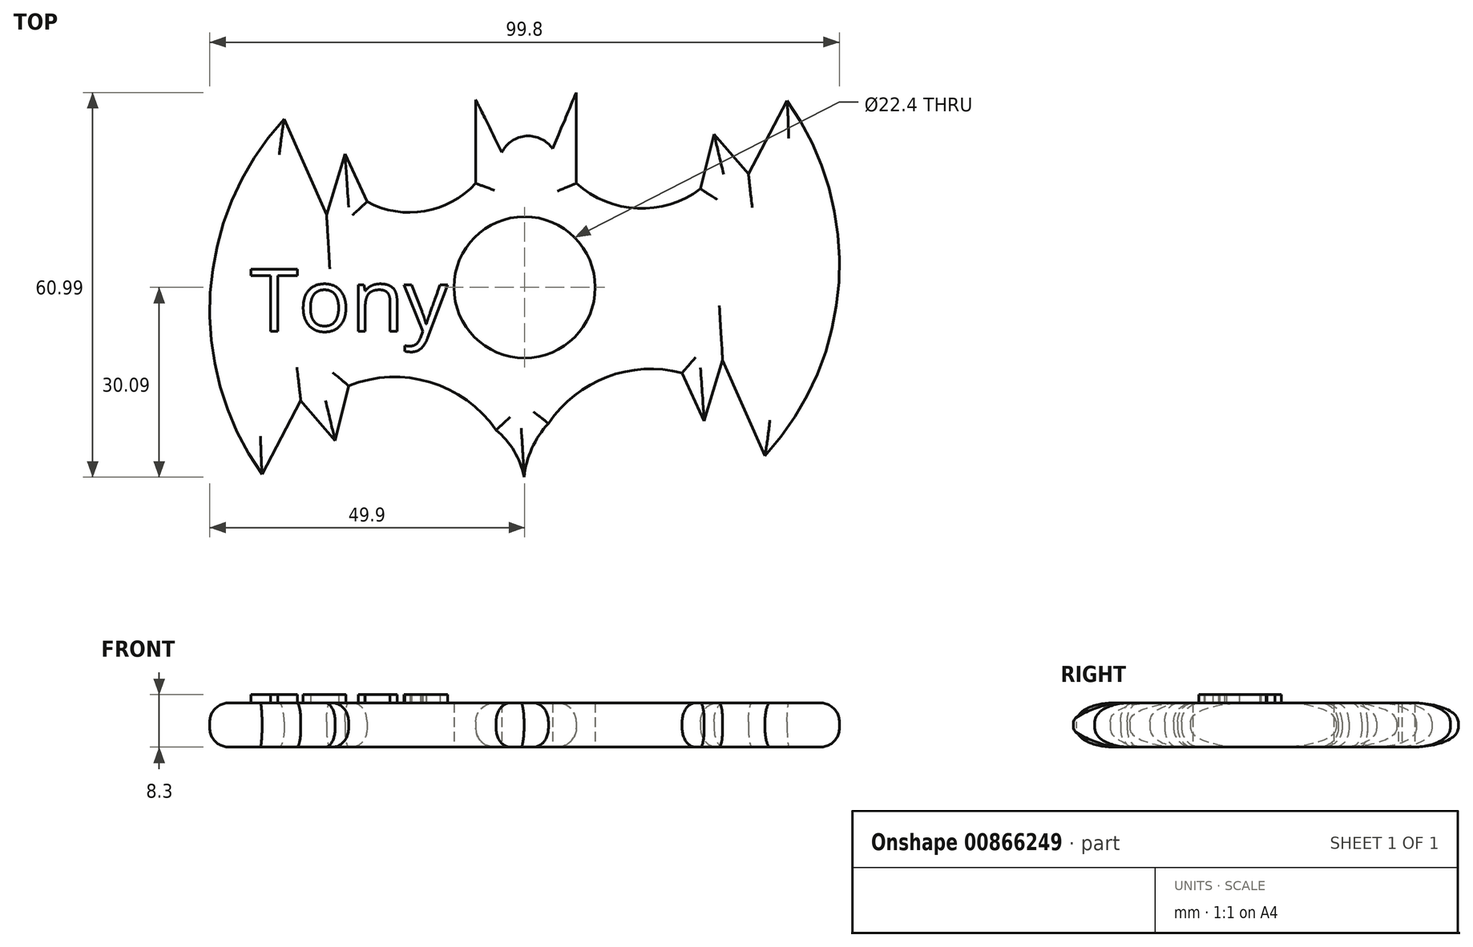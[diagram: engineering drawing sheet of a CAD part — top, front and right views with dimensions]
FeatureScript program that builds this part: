
annotation { "Feature Type Name" : "Feature", "Feature Type Description" : "" }
export const myFeature = defineFeature(function(context is Context, id is Id, definition is map)
    precondition{}
    {
        {
            var Q0;
            Q0=qCreatedBy(makeId("Top.planeOp"),FACE);
            var sketch = newSketch(context, id + "F0", { "sketchPlane" : qUnion([Q0])});
            skCircle(sketch, "E0", {"center": v(0, 0) * mm, "radius": 11.2 * mm});
            skCircle(sketch, "E1", {"center": v(0, 0) * mm, "radius": 13.2 * mm});
            skArc(sketch, "E2", {"start": v(-38.1, 26.72) * mm, "mid": v(-49.82, -0.84) * mm, "end": v(-41.61, -29.64) * mm});
            skArc(sketch, "E3.1.0", {"start": v(38.1, -26.72) * mm, "mid": v(49.82, 0.84) * mm, "end": v(41.61, 29.64) * mm});
            skLineSegment(sketch, "E4", {"start": v(-41.61, -29.64) * mm, "end": v(-35.48, -17.96) * mm});
            skLineSegment(sketch, "E5", {"start": v(-35.48, -17.96) * mm, "end": v(-35.48, -24.97) * mm});
            skArc(sketch, "E6", {"start": v(-4.53, -22.63) * mm, "mid": v(-14.98, -15.03) * mm, "end": v(-27.89, -15.62) * mm});
            skLineSegment(sketch, "E7.1.0", {"start": v(41.61, 29.64) * mm, "end": v(35.48, 17.96) * mm});
            skLineSegment(sketch, "E7.1.1", {"start": v(35.48, 17.96) * mm, "end": v(30.03, 24.29) * mm});
            skLineSegment(sketch, "E7.1.2", {"start": v(30.03, 24.29) * mm, "end": v(27.89, 15.62) * mm});
            skLineSegment(sketch, "E8", {"start": v(38.1, -26.72) * mm, "end": v(31.4, -11.53) * mm});
            skLineSegment(sketch, "E9", {"start": v(31.4, -11.53) * mm, "end": v(28.47, -21.17) * mm});
            skLineSegment(sketch, "E10", {"start": v(28.47, -21.17) * mm, "end": v(24.97, -13.58) * mm});
            skArc(sketch, "E11.1.0", {"start": v(-24.97, 13.58) * mm, "mid": v(-15.85, 12.08) * mm, "end": v(-7.74, 16.5) * mm});
            skLineSegment(sketch, "E11.1.2", {"start": v(-28.47, 21.17) * mm, "end": v(-24.97, 13.58) * mm});
            skLineSegment(sketch, "E11.1.4", {"start": v(-31.4, 11.53) * mm, "end": v(-28.47, 21.17) * mm});
            skLineSegment(sketch, "E11.1.5", {"start": v(-38.1, 26.72) * mm, "end": v(-31.4, 11.53) * mm});
            skArc(sketch, "E12", {"start": v(0, -34.06) * mm, "mid": v(-0.76, -27.75) * mm, "end": v(-4.53, -22.63) * mm});
            skArc(sketch, "E13.1.0", {"start": v(8.2, 16.53) * mm, "mid": v(17.88, 12.52) * mm, "end": v(27.89, 15.62) * mm});
            skLineSegment(sketch, "E14", {"start": v(-7.74, 16.5) * mm, "end": v(-7.74, 29.75) * mm});
            skLineSegment(sketch, "E15", {"start": v(-7.74, 29.75) * mm, "end": v(-3.6, 21.41) * mm});
            skLineSegment(sketch, "E16", {"start": v(8.2, 16.53) * mm, "end": v(8.2, 30.9) * mm});
            skLineSegment(sketch, "E17", {"start": v(8.2, 30.9) * mm, "end": v(4.45, 21.97) * mm});
            skArc(sketch, "E18", {"start": v(4.45, 21.97) * mm, "mid": v(0.27, 24) * mm, "end": v(-3.6, 21.41) * mm});
            skArc(sketch, "E19", {"start": v(24.97, -13.58) * mm, "mid": v(13.1, -14.2) * mm, "end": v(3.78, -21.57) * mm});
            skArc(sketch, "E20", {"start": v(3.78, -21.57) * mm, "mid": v(0.47, -27.38) * mm, "end": v(0, -34.06) * mm});
            skLineSegment(sketch, "E21.1.0", {"start": v(-35.48, -17.96) * mm, "end": v(-30.03, -24.29) * mm});
            skLineSegment(sketch, "E21.1.1", {"start": v(-30.03, -24.29) * mm, "end": v(-27.89, -15.62) * mm});
            skSolve(sketch);
        }
        {
            var Q0;
            Q0=makeQuery(id+"F0.imprint","IMPRINT",FACE,{"disambiguationData":[TD([[makeQuery(id+"F0.imprint","IMPRINT",EDGE,{"derivedFrom":sQuery(id+"F0.wireOp",EDGE,"E0")}),-1.0]])]});
            var Q1;
            Q1=makeQuery(id+"F0.imprint","IMPRINT",FACE,{"disambiguationData":[TD([[makeQuery(id+"F0.imprint","IMPRINT",EDGE,{"derivedFrom":sQuery(id+"F0.wireOp",EDGE,"E1")}),-1.0]])]});
            extrude(context, id + "F1", {"entities" : qUnion([Q0, Q1]), "depth" : 7 * mm, "offsetDistance" : 25 * mm});
        }
        {
            var Q0;
            Q0=makeQuery(id+"F1.opExtrude","CAP_EDGE",EDGE,{"disambiguationData":[OSD([sQuery(id+"F0.wireOp",EDGE,"E20")])],"isStart":false});
            var Q1;
            Q1=makeQuery(id+"F1.opExtrude","CAP_EDGE",EDGE,{"disambiguationData":[OSD([sQuery(id+"F0.wireOp",EDGE,"E19")])],"isStart":false});
            var Q2;
            Q2=makeQuery(id+"F1.opExtrude","CAP_EDGE",EDGE,{"disambiguationData":[OSD([sQuery(id+"F0.wireOp",EDGE,"E9")])],"isStart":false});
            var Q3;
            Q3=makeQuery(id+"F1.opExtrude","CAP_EDGE",EDGE,{"disambiguationData":[OSD([sQuery(id+"F0.wireOp",EDGE,"E3.1.0")])],"isStart":false});
            var Q4;
            Q4=makeQuery(id+"F1.opExtrude","CAP_EDGE",EDGE,{"disambiguationData":[OSD([sQuery(id+"F0.wireOp",EDGE,"E8")])],"isStart":false});
            var Q5;
            Q5=makeQuery(id+"F1.opExtrude","CAP_EDGE",EDGE,{"disambiguationData":[OSD([sQuery(id+"F0.wireOp",EDGE,"E7.1.0")])],"isStart":false});
            var Q6;
            Q6=makeQuery(id+"F1.opExtrude","CAP_EDGE",EDGE,{"disambiguationData":[OSD([sQuery(id+"F0.wireOp",EDGE,"E7.1.1")])],"isStart":false});
            var Q7;
            Q7=makeQuery(id+"F1.opExtrude","CAP_EDGE",EDGE,{"disambiguationData":[OSD([sQuery(id+"F0.wireOp",EDGE,"E7.1.2")])],"isStart":false});
            var Q8;
            Q8=makeQuery(id+"F1.opExtrude","CAP_EDGE",EDGE,{"disambiguationData":[OSD([sQuery(id+"F0.wireOp",EDGE,"E13.1.0")])],"isStart":false});
            var Q9;
            Q9=makeQuery(id+"F1.opExtrude","CAP_EDGE",EDGE,{"disambiguationData":[OSD([sQuery(id+"F0.wireOp",EDGE,"E16")])],"isStart":false});
            var Q10;
            Q10=makeQuery(id+"F1.opExtrude","CAP_EDGE",EDGE,{"disambiguationData":[OSD([sQuery(id+"F0.wireOp",EDGE,"E14")])],"isStart":false});
            var Q11;
            Q11=makeQuery(id+"F1.opExtrude","CAP_EDGE",EDGE,{"disambiguationData":[OSD([sQuery(id+"F0.wireOp",EDGE,"E11.1.0")])],"isStart":false});
            var Q12;
            Q12=makeQuery(id+"F1.opExtrude","CAP_EDGE",EDGE,{"disambiguationData":[OSD([sQuery(id+"F0.wireOp",EDGE,"E11.1.2")])],"isStart":false});
            var Q13;
            Q13=makeQuery(id+"F1.opExtrude","CAP_EDGE",EDGE,{"disambiguationData":[OSD([sQuery(id+"F0.wireOp",EDGE,"E11.1.5")])],"isStart":false});
            var Q14;
            Q14=makeQuery(id+"F1.opExtrude","CAP_EDGE",EDGE,{"disambiguationData":[OSD([sQuery(id+"F0.wireOp",EDGE,"E11.1.4")])],"isStart":false});
            var Q15;
            Q15=makeQuery(id+"F1.opExtrude","CAP_EDGE",EDGE,{"disambiguationData":[OSD([sQuery(id+"F0.wireOp",EDGE,"E2")])],"isStart":false});
            var Q16;
            Q16=makeQuery(id+"F1.opExtrude","CAP_EDGE",EDGE,{"disambiguationData":[OSD([sQuery(id+"F0.wireOp",EDGE,"E4")])],"isStart":false});
            var Q17;
            Q17=makeQuery(id+"F1.opExtrude","CAP_EDGE",EDGE,{"disambiguationData":[OSD([sQuery(id+"F0.wireOp",EDGE,"wEF84jsq-XExs-cQrN-D3yr-Ib7uIkRzdJAm")])],"isStart":false});
            var Q18;
            Q18=makeQuery(id+"F1.opExtrude","CAP_EDGE",EDGE,{"disambiguationData":[OSD([sQuery(id+"F0.wireOp",EDGE,"E12")])],"isStart":false});
            var Q19;
            Q19=makeQuery(id+"F1.opExtrude","CAP_EDGE",EDGE,{"disambiguationData":[OSD([sQuery(id+"F0.wireOp",EDGE,"E5")])],"isStart":false});
            var Q20;
            Q20=makeQuery(id+"F1.opExtrude","CAP_EDGE",EDGE,{"disambiguationData":[OSD([sQuery(id+"F0.wireOp",EDGE,"E10")])],"isStart":false});
            var Q21;
            Q21=makeQuery(id+"F1.opExtrude","CAP_EDGE",EDGE,{"disambiguationData":[OSD([sQuery(id+"F0.wireOp",EDGE,"E21.1.1")])],"isStart":false});
            var Q22;
            Q22=makeQuery(id+"F1.opExtrude","CAP_EDGE",EDGE,{"disambiguationData":[OSD([sQuery(id+"F0.wireOp",EDGE,"E6")])],"isStart":false});
            var Q23;
            Q23=makeQuery(id+"F1.opExtrude","CAP_EDGE",EDGE,{"disambiguationData":[OSD([sQuery(id+"F0.wireOp",EDGE,"E21.1.0")])],"isStart":false});
            var Q24;
            Q24=makeQuery(id+"F1.opExtrude","CAP_EDGE",EDGE,{"disambiguationData":[OSD([sQuery(id+"F0.wireOp",EDGE,"E3.1.0")])],"isStart":true});
            var Q25;
            Q25=makeQuery(id+"F1.opExtrude","CAP_EDGE",EDGE,{"disambiguationData":[OSD([sQuery(id+"F0.wireOp",EDGE,"E8")])],"isStart":true});
            var Q26;
            Q26=makeQuery(id+"F1.opExtrude","CAP_EDGE",EDGE,{"disambiguationData":[OSD([sQuery(id+"F0.wireOp",EDGE,"E9")])],"isStart":true});
            var Q27;
            Q27=makeQuery(id+"F1.opExtrude","CAP_EDGE",EDGE,{"disambiguationData":[OSD([sQuery(id+"F0.wireOp",EDGE,"E10")])],"isStart":true});
            var Q28;
            Q28=makeQuery(id+"F1.opExtrude","CAP_EDGE",EDGE,{"disambiguationData":[OSD([sQuery(id+"F0.wireOp",EDGE,"E19")])],"isStart":true});
            var Q29;
            Q29=makeQuery(id+"F1.opExtrude","CAP_EDGE",EDGE,{"disambiguationData":[OSD([sQuery(id+"F0.wireOp",EDGE,"E6")])],"isStart":true});
            var Q30;
            Q30=makeQuery(id+"F1.opExtrude","CAP_EDGE",EDGE,{"disambiguationData":[OSD([sQuery(id+"F0.wireOp",EDGE,"E12")])],"isStart":true});
            var Q31;
            Q31=makeQuery(id+"F1.opExtrude","CAP_EDGE",EDGE,{"disambiguationData":[OSD([sQuery(id+"F0.wireOp",EDGE,"E20")])],"isStart":true});
            var Q32;
            Q32=makeQuery(id+"F1.opExtrude","CAP_EDGE",EDGE,{"disambiguationData":[OSD([sQuery(id+"F0.wireOp",EDGE,"E21.1.1")])],"isStart":true});
            var Q33;
            Q33=makeQuery(id+"F1.opExtrude","CAP_EDGE",EDGE,{"disambiguationData":[OSD([sQuery(id+"F0.wireOp",EDGE,"E21.1.0")])],"isStart":true});
            var Q34;
            Q34=makeQuery(id+"F1.opExtrude","CAP_EDGE",EDGE,{"disambiguationData":[OSD([sQuery(id+"F0.wireOp",EDGE,"E4")])],"isStart":true});
            var Q35;
            Q35=makeQuery(id+"F1.opExtrude","CAP_EDGE",EDGE,{"disambiguationData":[OSD([sQuery(id+"F0.wireOp",EDGE,"E2")])],"isStart":true});
            var Q36;
            Q36=makeQuery(id+"F1.opExtrude","CAP_EDGE",EDGE,{"disambiguationData":[OSD([sQuery(id+"F0.wireOp",EDGE,"E11.1.5")])],"isStart":true});
            var Q37;
            Q37=makeQuery(id+"F1.opExtrude","CAP_EDGE",EDGE,{"disambiguationData":[OSD([sQuery(id+"F0.wireOp",EDGE,"E11.1.4")])],"isStart":true});
            var Q38;
            Q38=makeQuery(id+"F1.opExtrude","CAP_EDGE",EDGE,{"disambiguationData":[OSD([sQuery(id+"F0.wireOp",EDGE,"E14")])],"isStart":true});
            var Q39;
            Q39=makeQuery(id+"F1.opExtrude","CAP_EDGE",EDGE,{"disambiguationData":[OSD([sQuery(id+"F0.wireOp",EDGE,"E16")])],"isStart":true});
            var Q40;
            Q40=makeQuery(id+"F1.opExtrude","CAP_EDGE",EDGE,{"disambiguationData":[OSD([sQuery(id+"F0.wireOp",EDGE,"E13.1.0")])],"isStart":true});
            var Q41;
            Q41=makeQuery(id+"F1.opExtrude","CAP_EDGE",EDGE,{"disambiguationData":[OSD([sQuery(id+"F0.wireOp",EDGE,"E7.1.2")])],"isStart":true});
            var Q42;
            Q42=makeQuery(id+"F1.opExtrude","CAP_EDGE",EDGE,{"disambiguationData":[OSD([sQuery(id+"F0.wireOp",EDGE,"E7.1.1")])],"isStart":true});
            var Q43;
            Q43=makeQuery(id+"F1.opExtrude","CAP_EDGE",EDGE,{"disambiguationData":[OSD([sQuery(id+"F0.wireOp",EDGE,"E7.1.0")])],"isStart":true});
            var Q44;
            Q44=makeQuery(id+"F1.opExtrude","CAP_EDGE",EDGE,{"disambiguationData":[OSD([sQuery(id+"F0.wireOp",EDGE,"E11.1.0")])],"isStart":true});
            var Q45;
            Q45=makeQuery(id+"F1.opExtrude","CAP_EDGE",EDGE,{"disambiguationData":[OSD([sQuery(id+"F0.wireOp",EDGE,"E11.1.2")])],"isStart":true});
            fillet(context, id + "F2", {"entities" : qUnion([Q0, Q1, Q2, Q3, Q4, Q5, Q6, Q7, Q8, Q9, Q10, Q11, Q12, Q13, Q14, Q15, Q16, Q17, Q18, Q19, Q20, Q21, Q22, Q23, Q24, Q25, Q26, Q27, Q28, Q29, Q30, Q31, Q32, Q33, Q34, Q35, Q36, Q37, Q38, Q39, Q40, Q41, Q42, Q43, Q44, Q45]), "radius" : 3 * mm, "tangentPropagation" : true, "allowEdgeOverflow" : false});
        }
        {
            var Q0;
            Q0=qCreatedBy(makeId("Top.planeOp"),FACE);
            var sketch = newSketch(context, id + "F3", { "sketchPlane" : qUnion([Q0])});
            skText(sketch, "E22", { "text": "Tony", "fontName": "OpenSans-Regular.ttf"});
            const initialGuessF3  = {"E22": [-0.04348, -0.00694, 1, 0, 0.00991]};
            skSetInitialGuess(sketch, initialGuessF3);
            skSolve(sketch);
        }
        {
            var Q0;
            Q0 = qSketchRegion(id + "F3", true);
            extrude(context, id + "F4", {"entities" : qUnion([Q0]), "operationType" : NewBodyOperationType.ADD, "depth" : 8.3 * mm, "offsetDistance" : 25 * mm});
        }
    });
